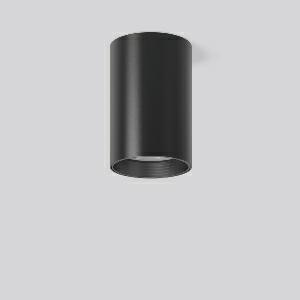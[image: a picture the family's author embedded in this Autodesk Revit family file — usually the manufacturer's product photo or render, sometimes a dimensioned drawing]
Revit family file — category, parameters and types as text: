
# Revit family: heledon_maxi_a_931227_003_3_ab5b
name_source: partatom
category: Lighting Fixtures
units: mm (PartAtom-declared; Revit-internal decimal feet)

## family parameters
Cut with Voids When Loaded = No
Host = Face
Light Source = No
Part Type = Normal
Room Calculation Point = No
Round Connector Dimension = Use Diameter
Shared = No

## types (1)
- HELEDON maxi A (1 x LED Modul 935, 3750 lm, 3500)
    Apparent Load = 35 VA
    Approval mark = CE
    CIE Flux Codes = 97 100 100 100 100
    Color Rendering = 92
    Color Temperature = 3500
    Default Elevation = 1800 mm
    Description = Series: HELEDON maxi
Cylindrical surface-mounted downlight. Housing: die-cast aluminium, powder-coated. Internal ceiling frame polycarbonate with bayonet mounting. Black plastic ring and recessed LED to prevent glare from the side. Optical assembly with lens made of plastic (polycarbonate) for the best homogeneous light distribution - can be changed without tools. Best colour rendering index Ra>90. Suitable for Ceiling mounting. Easy installation with a separate ceiling frame with bayonet mounting and plug connection. Driver integrated. Connected via plug-in connector. High quality converter without flickering and stroboscopic effect. The following accessories can be mounted without use of tools: interchangeable lenses, decorative glasses, honeycomb louvre, clear and frosted diffusers, white interchangeable plastic ring. 
Colour: deep black, matt (RAL 9005)
Diameter: 123 mm
Height: 183 mm
Lamp: LED
Socket: without socket
Colour temperature: 3500K
Colour rendering index (CRI): 92
System power: 35 W
Rated luminous flux: 3750 lm
Luminous efficiency: 107 lm/W
Control gear: Regulated power supply
Protection class: I
Type of protection: IP 20
    Height = 183 mm
    Lamp = 1 x LED Modul 935
    Lamp Light Flux = 3750 lm
    Lamp count = 1
    Length = 123 mm
    Lifetime = 50000 h
    Luminous efficacy = 107 lm/W
    Manufacturer = RZB
    ModVariant = No
    Model = 931227.003.3
    Mounting Place = Ceiling
    Mounting Type = Surface mounted
    Number of Poles = 1
    OnlyDefault = Yes
    Power Factor = 1
    Product Name = HELEDON maxi A
    Product group = Surface mounted downlights
    ProductGroupID = 302
    Protection Class = Protection class I
    Protection Degree = IP 20
    RLX_Detail_Level = 1
    RLX_Emergency_Light_Flux = 0 lm
    RLX_Emergency_Type = 0
    RLX_Emergency_Type_DB = No
    RlxData = <blob elided: 97341 chars, md5=4182c4d9>
    Socket = socket
    Standby Power = 0 W
    System Light Flux = 3750 lm
    System Power = 35 W
    Type Comments = Product without accessories
    Type Image = 931193.003.jpg
    URL = http://relux.com
    VarID = ---
    Voltage = 230 V
    Voltage Range = 220-240 V
    Weight = 0.00 kg
    Width = 0 mm  [stored 0 ft]

note: [stored X ft] marks values corroborated as IEEE doubles in the binary element streams (Revit-internal decimal feet)

## geometry (parser evidence)
native form markers: Blend x4, Sweep x9
no freeform markers — native parametric forms only
